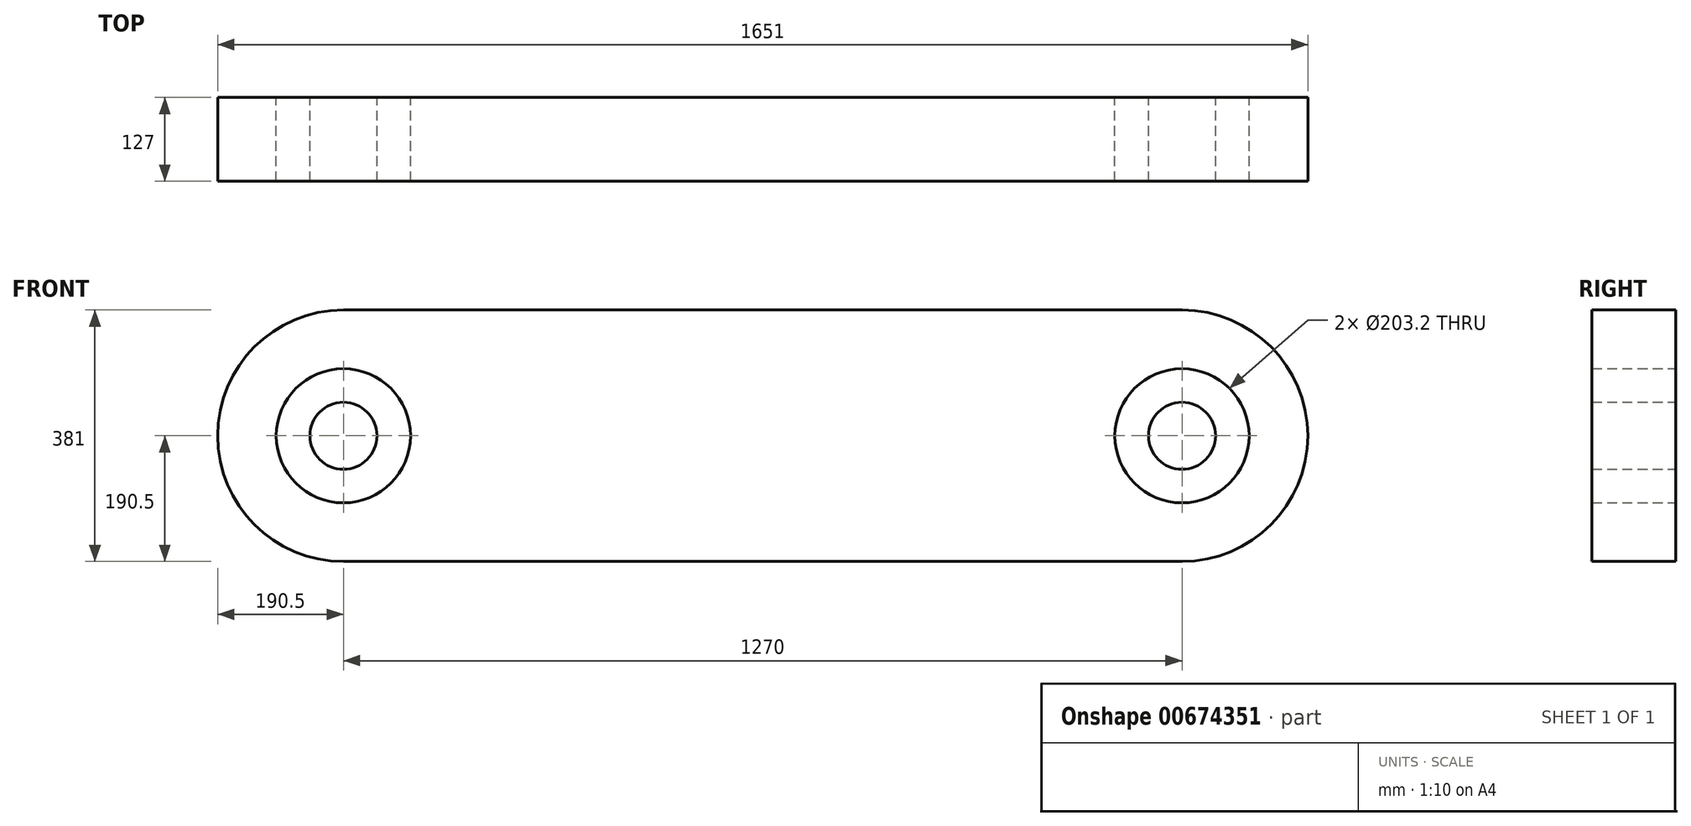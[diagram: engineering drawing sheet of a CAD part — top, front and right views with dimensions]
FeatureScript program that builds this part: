
annotation { "Feature Type Name" : "Feature", "Feature Type Description" : "" }
export const myFeature = defineFeature(function(context is Context, id is Id, definition is map)
    precondition{}
    {
        {
            var Q0;
            Q0=qCreatedBy(makeId("Front.planeOp"),FACE);
            var sketch = newSketch(context, id + "F0", { "sketchPlane" : qUnion([Q0])});
            skLineSegment(sketch, "E0.bottom", {"start": v(0, 0) * mm, "end": v(1270, 0) * mm});
            skLineSegment(sketch, "E0.top", {"start": v(0, 381) * mm, "end": v(1270, 381) * mm});
            skArc(sketch, "E1", {"start": v(0, 381) * mm, "mid": v(-190.5, 190.5) * mm, "end": v(0, 0) * mm});
            skArc(sketch, "E2", {"start": v(1270, 0) * mm, "mid": v(1460.5, 190.5) * mm, "end": v(1270, 381) * mm});
            skCircle(sketch, "E3", {"center": v(0, 190.5) * mm, "radius": 101.6 * mm});
            skCircle(sketch, "E4", {"center": v(1270, 190.5) * mm, "radius": 101.6 * mm});
            skCircle(sketch, "E5", {"center": v(1270, 190.5) * mm, "radius": 50.8 * mm});
            skCircle(sketch, "E6", {"center": v(0, 190.5) * mm, "radius": 50.8 * mm});
            skSolve(sketch);
        }
        {
            var Q0;
            Q0=makeQuery(id+"F0.imprint","IMPRINT",FACE,{"disambiguationData":[TD([[makeQuery(id+"F0.imprint","IMPRINT",EDGE,{"derivedFrom":sQuery(id+"F0.wireOp",EDGE,"E0.bottom")}),1.0]])]});
            var Q1;
            Q1=makeQuery(id+"F0.imprint","IMPRINT",FACE,{"disambiguationData":[TD([[makeQuery(id+"F0.imprint","IMPRINT",EDGE,{"derivedFrom":sQuery(id+"F0.wireOp",EDGE,"E6")}),1.0]])]});
            var Q2;
            Q2=makeQuery(id+"F0.imprint","IMPRINT",FACE,{"disambiguationData":[TD([[makeQuery(id+"F0.imprint","IMPRINT",EDGE,{"derivedFrom":sQuery(id+"F0.wireOp",EDGE,"E5")}),1.0]])]});
            extrude(context, id + "F1", {"entities" : qUnion([Q0, Q1, Q2]), "depth" : 127 * mm, "offsetDistance" : 25.4 * mm});
        }
    });
